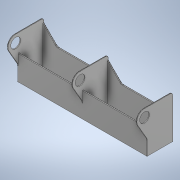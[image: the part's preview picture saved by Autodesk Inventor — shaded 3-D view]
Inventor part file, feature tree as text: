
AUTODESK INVENTOR PART (.ipt)
format: ipt  version: 2021 (Build 250183000, 183)  size: 388,608 bytes
history: native  units: mm
features: extrude x4, sketch x3, fillet x3, projected_geometry x2, pattern_linear x1
ambient origin geometry x8: Origin, YZ Plane, XZ Plane, XY Plane, X Axis, Y Axis, Z Axis, Center Point
bodies: Solid1 (feature_tree)
feature tree (13):
  sketch  "Sketch1"  dims[d0=1.2mm d1=0.8mm]
  extrude  "Extrusion1"  Depth=0.8mm
  extrude  "Extrusion2"  Depth=24.0mm
  sketch  "Sketch2"  dims[d2=0.8mm d3=24.0mm d4=65.0mm]
  fillet  "Fillet1"  Radius=65.0mm
  extrude  "Extrusion3"  Depth=0.25mm
  pattern_linear  "Rectangular Pattern1"  Spacing1=0.35mm  [1 undecoded]
  extrude  "Extrusion4"  Depth=0.25mm TaperAngle=0.0deg
  fillet  "Fillet2"  Radius=1.0mm
  fillet  "Fillet3"  Radius=0.5mm
  projected_geometry  "Projected Loop1"
  sketch  "Sketch3"  dims[d5=132.75mm d6=0.8mm d7=0.35mm d8=25.0mm d9=0.0mm d10=1.0mm d11=0.0mm d12=0.5mm d13=26.2mm d14=95.6mm d15=108.4mm d16=0.5mm d17=43.0mm d18=3.0mm d19=10.0mm d20=18.0mm d21=3.0mm d22=0.8mm d23=0.0mm d24=65.8mm d25=30.0mm d27=65.8mm d28=45.0deg d29=4.0mm d30=1.0mm d31=0.0mm d32=0.5mm d33=5.0mm d34=0.5mm d35=0.25mm]
  projected_geometry  "Projected Loop2"
note: 1 required parameter value undecoded (feature->parameter linkage not recoverable at this tier; creation-order binding heuristic only, values carry confidence <= 0.55)
